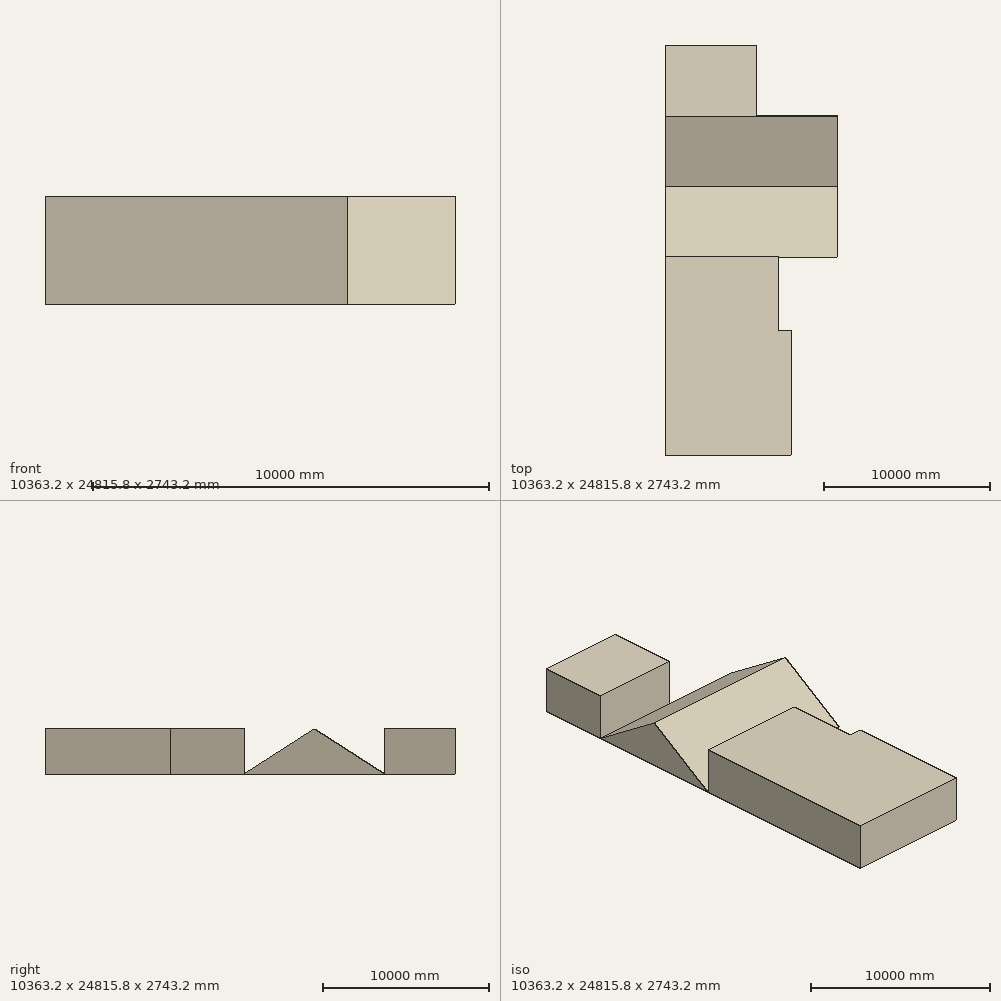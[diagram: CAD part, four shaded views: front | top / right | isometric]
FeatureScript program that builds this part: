
annotation { "Feature Type Name" : "Feature", "Feature Type Description" : "" }
export const myFeature = defineFeature(function(context is Context, id is Id, definition is map)
    precondition{}
    {
        {
            var Q0;
            Q0=qCreatedBy(makeId("Top.planeOp"),FACE);
            var sketch = newSketch(context, id + "F0", { "sketchPlane" : qUnion([Q0])});
            skLineSegment(sketch, "E0", {"start": v(0, 0) * mm, "end": v(7620, 0) * mm});
            skLineSegment(sketch, "E1", {"start": v(7620, 0) * mm, "end": v(7620, 7569.2) * mm});
            skLineSegment(sketch, "E2", {"start": v(0, 0) * mm, "end": v(0, 24815.8) * mm});
            skLineSegment(sketch, "E3", {"start": v(0, 24815.8) * mm, "end": v(5486.4, 24815.8) * mm});
            skLineSegment(sketch, "E4", {"start": v(5486.4, 24815.8) * mm, "end": v(5486.4, 20548.6) * mm});
            skLineSegment(sketch, "E5", {"start": v(5486.4, 20548.6) * mm, "end": v(10363.2, 20548.6) * mm});
            skLineSegment(sketch, "E6", {"start": v(10363.2, 20548.6) * mm, "end": v(10363.2, 12014.2) * mm});
            skLineSegment(sketch, "E7", {"start": v(10363.2, 12014.2) * mm, "end": v(6832.6, 12014.2) * mm});
            skLineSegment(sketch, "E8", {"start": v(6832.6, 12014.2) * mm, "end": v(6832.6, 7569.2) * mm});
            skLineSegment(sketch, "E9", {"start": v(6832.6, 7569.2) * mm, "end": v(7620, 7569.2) * mm});
            skSolve(sketch);
        }
        {
            var Q0;
            Q0 = qSketchRegion(id + "F0", true);
            extrude(context, id + "F1", {"entities" : qUnion([Q0]), "depth" : 2743.2 * mm});
        }
        {
            var Q0;
            Q0=makeQuery(id+"F1.opExtrude","SWEPT_FACE",FACE,{"disambiguationData":[OSD([sQuery(id+"F0.wireOp",EDGE,"E6")])]});
            var sketch = newSketch(context, id + "F2", { "sketchPlane" : qUnion([Q0])});
            skLineSegment(sketch, "E10", {"start": v(16281.4, 2743.2) * mm, "end": v(12014.2, 0) * mm});
            skLineSegment(sketch, "E11", {"start": v(12014.2, 0) * mm, "end": v(12014.2, 2743.2) * mm});
            skLineSegment(sketch, "E12", {"start": v(12014.2, 2743.2) * mm, "end": v(20548.6, 2743.2) * mm});
            skLineSegment(sketch, "E13", {"start": v(20548.6, 2743.2) * mm, "end": v(20548.6, 0) * mm});
            skLineSegment(sketch, "E14", {"start": v(20548.6, 0) * mm, "end": v(16281.4, 2743.2) * mm});
            skSolve(sketch);
        }
        {
            var Q0;
            Q0 = qSketchRegion(id + "F2", true);
            extrude(context, id + "F3", {"entities" : qUnion([Q0]), "operationType" : NewBodyOperationType.REMOVE, "endBound" : BoundingType.THROUGH_ALL, "oppositeDirection" : true, "depth" : 25.4 * mm});
        }
    });
